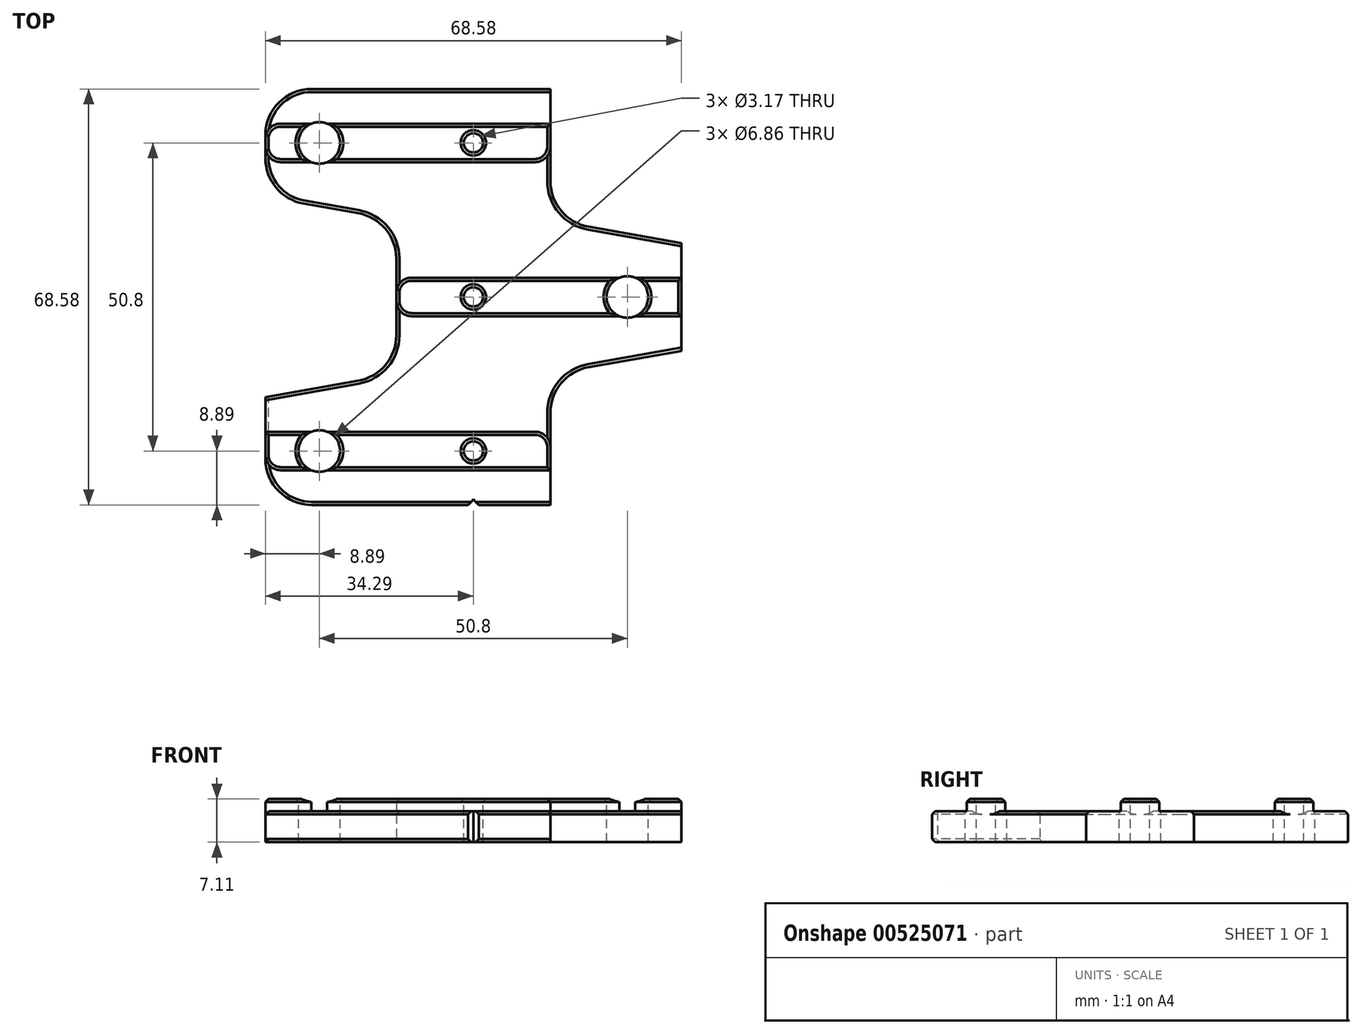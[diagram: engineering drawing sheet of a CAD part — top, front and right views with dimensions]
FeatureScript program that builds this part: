
annotation { "Feature Type Name" : "Feature", "Feature Type Description" : "" }
export const myFeature = defineFeature(function(context is Context, id is Id, definition is map)
    precondition{}
    {
        {
            var Q0;
            Q0=qCreatedBy(makeId("Right.planeOp"),FACE);
            var sketch = newSketch(context, id + "F0", { "sketchPlane" : qUnion([Q0])});
            skLineSegment(sketch, "E0.bottom", {"start": v(-34.3, 5.08) * mm, "end": v(-28.58, 5.08) * mm});
            skLineSegment(sketch, "E0.top", {"start": v(-34.3, 0) * mm, "end": v(34.3, 0) * mm});
            skLineSegment(sketch, "E0.left", {"start": v(-34.3, 5.08) * mm, "end": v(-34.3, 0) * mm});
            skLineSegment(sketch, "E0.right", {"start": v(34.3, 5.08) * mm, "end": v(34.3, 0) * mm});
            skLineSegment(sketch, "E1.bottom", {"start": v(-3.18, 7.11) * mm, "end": v(3.18, 7.11) * mm});
            skLineSegment(sketch, "E1.left", {"start": v(-3.18, 7.11) * mm, "end": v(-3.18, 5.08) * mm});
            skLineSegment(sketch, "E1.right", {"start": v(3.18, 7.11) * mm, "end": v(3.18, 5.08) * mm});
            skLineSegment(sketch, "E2.bottom", {"start": v(22.23, 7.11) * mm, "end": v(28.58, 7.11) * mm});
            skLineSegment(sketch, "E2.left", {"start": v(22.23, 7.11) * mm, "end": v(22.23, 5.08) * mm});
            skLineSegment(sketch, "E2.right", {"start": v(28.58, 7.11) * mm, "end": v(28.58, 5.08) * mm});
            skLineSegment(sketch, "E3.bottom", {"start": v(-28.58, 7.11) * mm, "end": v(-22.23, 7.11) * mm});
            skLineSegment(sketch, "E3.left", {"start": v(-28.58, 7.11) * mm, "end": v(-28.58, 5.08) * mm});
            skLineSegment(sketch, "E3.right", {"start": v(-22.23, 7.11) * mm, "end": v(-22.23, 5.08) * mm});
            skLineSegment(sketch, "E4.trimOffspring", {"start": v(-22.23, 5.08) * mm, "end": v(-3.18, 5.08) * mm});
            skLineSegment(sketch, "E5.trimOffspring", {"start": v(3.18, 5.08) * mm, "end": v(22.23, 5.08) * mm});
            skLineSegment(sketch, "E6.trimOffspring", {"start": v(28.58, 5.08) * mm, "end": v(34.3, 5.08) * mm});
            skSolve(sketch);
        }
        {
            var Q0;
            Q0 = qSketchRegion(id + "F0", true);
            extrude(context, id + "F1", {"entities" : qUnion([Q0]), "endBound" : BoundingType.SYMMETRIC, "depth" : 68.58 * mm, "offsetDistance" : 25.4 * mm, "hasSecondDirection" : true, "secondDirectionOppositeDirection" : true, "secondDirectionDepth" : 25.4 * mm});
        }
        {
            var Q0;
            Q0=qCreatedBy(makeId("Top.planeOp"),FACE);
            var sketch = newSketch(context, id + "F2", { "sketchPlane" : qUnion([Q0])});
            skLineSegment(sketch, "E7", {"start": v(-34.3, 16.51) * mm, "end": v(-12.7, 12.7) * mm});
            skLineSegment(sketch, "E8", {"start": v(-12.7, 12.7) * mm, "end": v(-12.7, -12.7) * mm});
            skLineSegment(sketch, "E9", {"start": v(-12.7, -12.7) * mm, "end": v(-34.3, -16.51) * mm});
            skLineSegment(sketch, "E10", {"start": v(-34.3, -16.51) * mm, "end": v(-34.3, 16.51) * mm});
            skSolve(sketch);
        }
        {
            var Q0;
            Q0 = qSketchRegion(id + "F2", true);
            extrude(context, id + "F3", {"entities" : qUnion([Q0]), "operationType" : NewBodyOperationType.REMOVE, "endBound" : BoundingType.THROUGH_ALL, "depth" : 25.4 * mm, "offsetDistance" : 25.4 * mm});
        }
        {
            var Q0;
            Q0=qCreatedBy(makeId("Top.planeOp"),FACE);
            var sketch = newSketch(context, id + "F4", { "sketchPlane" : qUnion([Q0])});
            skLineSegment(sketch, "E11", {"start": v(34.62, 34.3) * mm, "end": v(12.7, 34.3) * mm});
            skLineSegment(sketch, "E12", {"start": v(12.7, 34.3) * mm, "end": v(12.7, 12.7) * mm});
            skLineSegment(sketch, "E13", {"start": v(12.7, 12.7) * mm, "end": v(34.3, 8.9) * mm});
            skLineSegment(sketch, "E14", {"start": v(34.3, 8.9) * mm, "end": v(34.3, -8.9) * mm});
            skLineSegment(sketch, "E15", {"start": v(34.3, -8.9) * mm, "end": v(12.7, -12.7) * mm});
            skLineSegment(sketch, "E16", {"start": v(12.7, -12.7) * mm, "end": v(12.7, -34.3) * mm});
            skLineSegment(sketch, "E17", {"start": v(12.7, -34.3) * mm, "end": v(34.62, -34.3) * mm});
            skLineSegment(sketch, "E18", {"start": v(34.62, -34.3) * mm, "end": v(34.62, 34.3) * mm});
            skSolve(sketch);
        }
        {
            var Q0;
            Q0 = qSketchRegion(id + "F4", true);
            extrude(context, id + "F5", {"entities" : qUnion([Q0]), "operationType" : NewBodyOperationType.REMOVE, "endBound" : BoundingType.THROUGH_ALL, "depth" : 25.4 * mm, "offsetDistance" : 25.4 * mm});
        }
        {
            var Q0;
            Q0=makeQuery(id+"F1.opExtrude","SWEPT_FACE",FACE,{"disambiguationData":[OSD([sQuery(id+"F0.wireOp",EDGE,"E1.bottom")])]});
            var sketch = newSketch(context, id + "F6", { "sketchPlane" : qUnion([Q0])});
            skPoint(sketch, "E19", {"position": v(0, 0) * mm});
            skPoint(sketch, "E20", {"position": v(0, 25.4) * mm});
            skPoint(sketch, "E21", {"position": v(0, -25.4) * mm});
            skLineSegment(sketch, "E22", {"start": v(-34.3, 25.4) * mm, "end": v(12.7, 25.4) * mm, "construction": true});
            skLineSegment(sketch, "E23", {"start": v(-34.3, -25.4) * mm, "end": v(12.7, -25.4) * mm, "construction": true});
            skPoint(sketch, "E24", {"position": v(-25.4, 25.4) * mm});
            skPoint(sketch, "E25", {"position": v(25.4, 0) * mm});
            skPoint(sketch, "E26", {"position": v(-25.4, -25.4) * mm});
            skSolve(sketch);
        }
        {
            var Q0;
            Q0=sQuery(id+"F6.wireOp",VERTEX,"E20");
            var Q1;
            Q1=sQuery(id+"F6.wireOp",VERTEX,"E19");
            var Q2;
            Q2=sQuery(id+"F6.wireOp",VERTEX,"E21");
            var Q3;
            Q3=makeQuery(id+"F1.opExtrude","SWEPT_BODY",BODY,{"disambiguationData":[OSD([sQuery(id+"F0.wireOp",EDGE,"E0.bottom"),sQuery(id+"F0.wireOp",EDGE,"E0.top"),sQuery(id+"F0.wireOp",EDGE,"E0.left"),sQuery(id+"F0.wireOp",EDGE,"E0.right"),sQuery(id+"F0.wireOp",EDGE,"E1.bottom"),sQuery(id+"F0.wireOp",EDGE,"E1.left"),sQuery(id+"F0.wireOp",EDGE,"E1.right"),sQuery(id+"F0.wireOp",EDGE,"E2.bottom"),sQuery(id+"F0.wireOp",EDGE,"E2.left"),sQuery(id+"F0.wireOp",EDGE,"E2.right"),sQuery(id+"F0.wireOp",EDGE,"E3.bottom"),sQuery(id+"F0.wireOp",EDGE,"E3.left"),sQuery(id+"F0.wireOp",EDGE,"E3.right"),sQuery(id+"F0.wireOp",EDGE,"E4.trimOffspring"),sQuery(id+"F0.wireOp",EDGE,"E5.trimOffspring"),sQuery(id+"F0.wireOp",EDGE,"E6.trimOffspring")])]});
            hole(context, id + "F7", {"style" : HoleStyle.SIMPLE, "endStyle" : HoleEndStyle.THROUGH, "holeDiameter" : 3.17 * mm, "tappedDepth" : 12.7 * mm, "tapClearance" : 3, "startFromSketch" : true, "locations" : qUnion([Q0, Q1, Q2]), "scope" : qUnion([Q3])});
        }
        {
            var Q0;
            Q0=sQuery(id+"F6.wireOp",VERTEX,"E24");
            var Q1;
            Q1=sQuery(id+"F6.wireOp",VERTEX,"E25");
            var Q2;
            Q2=sQuery(id+"F6.wireOp",VERTEX,"E26");
            var Q3;
            Q3=makeQuery(id+"F1.opExtrude","SWEPT_BODY",BODY,{"disambiguationData":[OSD([sQuery(id+"F0.wireOp",EDGE,"E0.bottom"),sQuery(id+"F0.wireOp",EDGE,"E0.top"),sQuery(id+"F0.wireOp",EDGE,"E0.left"),sQuery(id+"F0.wireOp",EDGE,"E0.right"),sQuery(id+"F0.wireOp",EDGE,"E1.bottom"),sQuery(id+"F0.wireOp",EDGE,"E1.left"),sQuery(id+"F0.wireOp",EDGE,"E1.right"),sQuery(id+"F0.wireOp",EDGE,"E2.bottom"),sQuery(id+"F0.wireOp",EDGE,"E2.left"),sQuery(id+"F0.wireOp",EDGE,"E2.right"),sQuery(id+"F0.wireOp",EDGE,"E3.bottom"),sQuery(id+"F0.wireOp",EDGE,"E3.left"),sQuery(id+"F0.wireOp",EDGE,"E3.right"),sQuery(id+"F0.wireOp",EDGE,"E4.trimOffspring"),sQuery(id+"F0.wireOp",EDGE,"E5.trimOffspring"),sQuery(id+"F0.wireOp",EDGE,"E6.trimOffspring")])]});
            hole(context, id + "F8", {"style" : HoleStyle.SIMPLE, "endStyle" : HoleEndStyle.THROUGH, "holeDiameter" : 6.86 * mm, "tappedDepth" : 12.7 * mm, "tapClearance" : 3, "startFromSketch" : true, "locations" : qUnion([Q0, Q1, Q2]), "scope" : qUnion([Q3])});
        }
        {
            var Q0;
            Q0=makeQuery(id+"F3.boolean.opBoolean","COPY",EDGE,{"derivedFrom":makeQuery(id+"F3.opExtrude","SWEPT_EDGE",EDGE,{"disambiguationData":[OSD([sQuery(id+"F2.wireOp",EDGE,"E8"),sQuery(id+"F2.wireOp",EDGE,"E9")])]})});
            var Q1;
            Q1=makeQuery(id+"F3.boolean.opBoolean","COPY",EDGE,{"derivedFrom":makeQuery(id+"F3.opExtrude","SWEPT_EDGE",EDGE,{"disambiguationData":[OSD([sQuery(id+"F2.wireOp",EDGE,"E9"),sQuery(id+"F2.wireOp",EDGE,"E10")])]})});
            var Q2;
            Q2=makeQuery(id+"F1.opExtrude","CAP_EDGE",EDGE,{"disambiguationData":[OSD([sQuery(id+"F0.wireOp",EDGE,"E0.left")])],"isStart":true});
            var Q3;
            Q3=makeQuery(id+"F3.boolean.opBoolean","COPY",EDGE,{"derivedFrom":makeQuery(id+"F3.opExtrude","SWEPT_EDGE",EDGE,{"disambiguationData":[OSD([sQuery(id+"F2.wireOp",EDGE,"E7"),sQuery(id+"F2.wireOp",EDGE,"E10")])]})});
            var Q4;
            Q4=makeQuery(id+"F1.opExtrude","CAP_EDGE",EDGE,{"disambiguationData":[OSD([sQuery(id+"F0.wireOp",EDGE,"E0.right")])],"isStart":true});
            var Q5;
            Q5=makeQuery(id+"F5.boolean.opBoolean","COPY",EDGE,{"derivedFrom":makeQuery(id+"F5.opExtrude","SWEPT_EDGE",EDGE,{"disambiguationData":[OSD([sQuery(id+"F4.wireOp",EDGE,"E11"),sQuery(id+"F4.wireOp",EDGE,"E12")])]})});
            var Q6;
            Q6=makeQuery(id+"F5.boolean.opBoolean","COPY",EDGE,{"derivedFrom":makeQuery(id+"F5.opExtrude","SWEPT_EDGE",EDGE,{"disambiguationData":[OSD([sQuery(id+"F4.wireOp",EDGE,"E13"),sQuery(id+"F4.wireOp",EDGE,"E14")])]})});
            var Q7;
            Q7=makeQuery(id+"F5.boolean.opBoolean","COPY",EDGE,{"derivedFrom":makeQuery(id+"F5.opExtrude","SWEPT_EDGE",EDGE,{"disambiguationData":[OSD([sQuery(id+"F4.wireOp",EDGE,"E12"),sQuery(id+"F4.wireOp",EDGE,"E13")])]})});
            var Q8;
            Q8=makeQuery(id+"F5.boolean.opBoolean","COPY",EDGE,{"derivedFrom":makeQuery(id+"F5.opExtrude","SWEPT_EDGE",EDGE,{"disambiguationData":[OSD([sQuery(id+"F4.wireOp",EDGE,"E16"),sQuery(id+"F4.wireOp",EDGE,"E17")])]})});
            var Q9;
            Q9=makeQuery(id+"F5.boolean.opBoolean","COPY",EDGE,{"derivedFrom":makeQuery(id+"F5.opExtrude","SWEPT_EDGE",EDGE,{"disambiguationData":[OSD([sQuery(id+"F4.wireOp",EDGE,"E15"),sQuery(id+"F4.wireOp",EDGE,"E16")])]})});
            var Q10;
            Q10=makeQuery(id+"F5.boolean.opBoolean","COPY",EDGE,{"derivedFrom":makeQuery(id+"F5.opExtrude","SWEPT_EDGE",EDGE,{"disambiguationData":[OSD([sQuery(id+"F4.wireOp",EDGE,"E14"),sQuery(id+"F4.wireOp",EDGE,"E15")])]})});
            var Q11;
            Q11=makeQuery(id+"F3.boolean.opBoolean","COPY",EDGE,{"derivedFrom":makeQuery(id+"F3.opExtrude","SWEPT_EDGE",EDGE,{"disambiguationData":[OSD([sQuery(id+"F2.wireOp",EDGE,"E7"),sQuery(id+"F2.wireOp",EDGE,"E8")])]})});
            fillet(context, id + "F9", {"entities" : qUnion([Q0, Q1, Q2, Q3, Q4, Q5, Q6, Q7, Q8, Q9, Q10, Q11]), "radius" : 7.62 * mm, "tangentPropagation" : true, "allowEdgeOverflow" : false});
        }
        {
            var Q0;
            {var subQ0=sQuery(id+"F4.wireOp",EDGE,"E16");Q0=makeQuery(id+"F9.opFillet","BLEND_EDGE",EDGE,{"blendedFrom":[makeQuery(id+"F5.boolean.opBoolean","COPY",EDGE,{"derivedFrom":makeQuery(id+"F5.opExtrude","SWEPT_EDGE",EDGE,{"disambiguationData":[OSD([subQ0,sQuery(id+"F4.wireOp",EDGE,"E17")])]})}),makeQuery(id+"F8.hole-2.boolean.opBoolean","SPLIT",FACE,{"disambiguationData":[TD([makeQuery(id+"F5.boolean.opBoolean","COPY",FACE,{"derivedFrom":makeQuery(id+"F5.opExtrude","SWEPT_FACE",FACE,{"disambiguationData":[OSD([subQ0])]})})])],"derivedFrom":makeQuery(id+"F1.opExtrude","SWEPT_FACE",FACE,{"disambiguationData":[OSD([sQuery(id+"F0.wireOp",EDGE,"E3.left")])]})})],"blendedInto":[makeQuery(id+"F8.hole-2.boolean.opBoolean","SPLIT",FACE,{"disambiguationData":[TD([makeQuery(id+"F5.boolean.opBoolean","COPY",FACE,{"derivedFrom":makeQuery(id+"F5.opExtrude","SWEPT_FACE",FACE,{"disambiguationData":[OSD([subQ0])]})})])],"derivedFrom":makeQuery(id+"F1.opExtrude","SWEPT_FACE",FACE,{"disambiguationData":[OSD([sQuery(id+"F0.wireOp",EDGE,"E3.left")])]})})]});}
            var Q1;
            Q1=makeQuery(id+"F5.boolean.opBoolean","INTERSECT",EDGE,{"derivedFrom":[makeQuery(id+"F1.opExtrude","SWEPT_FACE",FACE,{"disambiguationData":[OSD([sQuery(id+"F0.wireOp",EDGE,"E3.right")])]}),makeQuery(id+"F5.opExtrude","SWEPT_FACE",FACE,{"disambiguationData":[OSD([sQuery(id+"F4.wireOp",EDGE,"E16")])]})]});
            var Q2;
            {var subQ0=sQuery(id+"F0.wireOp",EDGE,"E4.trimOffspring");var subQ1=sQuery(id+"F0.wireOp",EDGE,"E1.left");var subQ2=sQuery(id+"F0.wireOp",EDGE,"E1.bottom");Q2=makeQuery(id+"F9.opFillet","BLEND_EDGE",EDGE,{"blendedFrom":[makeQuery(id+"F5.boolean.opBoolean","COPY",EDGE,{"derivedFrom":makeQuery(id+"F5.opExtrude","SWEPT_EDGE",EDGE,{"disambiguationData":[OSD([sQuery(id+"F4.wireOp",EDGE,"E14"),sQuery(id+"F4.wireOp",EDGE,"E15")])]})}),makeQuery(id+"F8.hole-1.boolean.opBoolean","SPLIT",FACE,{"disambiguationData":[TD([makeQuery(id+"F1.opExtrude","CAP_FACE",FACE,{"disambiguationData":[OSD([sQuery(id+"F0.wireOp",EDGE,"E0.bottom"),sQuery(id+"F0.wireOp",EDGE,"E0.top"),sQuery(id+"F0.wireOp",EDGE,"E0.left"),sQuery(id+"F0.wireOp",EDGE,"E0.right"),subQ2,subQ1,sQuery(id+"F0.wireOp",EDGE,"E1.right"),sQuery(id+"F0.wireOp",EDGE,"E2.bottom"),sQuery(id+"F0.wireOp",EDGE,"E2.left"),sQuery(id+"F0.wireOp",EDGE,"E2.right"),sQuery(id+"F0.wireOp",EDGE,"E3.bottom"),sQuery(id+"F0.wireOp",EDGE,"E3.left"),sQuery(id+"F0.wireOp",EDGE,"E3.right"),subQ0,sQuery(id+"F0.wireOp",EDGE,"E5.trimOffspring"),sQuery(id+"F0.wireOp",EDGE,"E6.trimOffspring")])],"isStart":false})])],"derivedFrom":makeQuery(id+"F1.opExtrude","SWEPT_FACE",FACE,{"disambiguationData":[OSD([subQ1])]})})],"blendedInto":[makeQuery(id+"F8.hole-1.boolean.opBoolean","SPLIT",FACE,{"disambiguationData":[TD([makeQuery(id+"F1.opExtrude","CAP_FACE",FACE,{"disambiguationData":[OSD([sQuery(id+"F0.wireOp",EDGE,"E0.bottom"),sQuery(id+"F0.wireOp",EDGE,"E0.top"),sQuery(id+"F0.wireOp",EDGE,"E0.left"),sQuery(id+"F0.wireOp",EDGE,"E0.right"),subQ2,subQ1,sQuery(id+"F0.wireOp",EDGE,"E1.right"),sQuery(id+"F0.wireOp",EDGE,"E2.bottom"),sQuery(id+"F0.wireOp",EDGE,"E2.left"),sQuery(id+"F0.wireOp",EDGE,"E2.right"),sQuery(id+"F0.wireOp",EDGE,"E3.bottom"),sQuery(id+"F0.wireOp",EDGE,"E3.left"),sQuery(id+"F0.wireOp",EDGE,"E3.right"),subQ0,sQuery(id+"F0.wireOp",EDGE,"E5.trimOffspring"),sQuery(id+"F0.wireOp",EDGE,"E6.trimOffspring")])],"isStart":false})])],"derivedFrom":makeQuery(id+"F1.opExtrude","SWEPT_FACE",FACE,{"disambiguationData":[OSD([subQ1])]})})]});}
            var Q3;
            {var subQ0=sQuery(id+"F0.wireOp",EDGE,"E5.trimOffspring");var subQ1=sQuery(id+"F0.wireOp",EDGE,"E1.right");var subQ2=sQuery(id+"F0.wireOp",EDGE,"E1.bottom");Q3=makeQuery(id+"F9.opFillet","BLEND_EDGE",EDGE,{"blendedFrom":[makeQuery(id+"F5.boolean.opBoolean","COPY",EDGE,{"derivedFrom":makeQuery(id+"F5.opExtrude","SWEPT_EDGE",EDGE,{"disambiguationData":[OSD([sQuery(id+"F4.wireOp",EDGE,"E13"),sQuery(id+"F4.wireOp",EDGE,"E14")])]})}),makeQuery(id+"F8.hole-1.boolean.opBoolean","SPLIT",FACE,{"disambiguationData":[TD([makeQuery(id+"F1.opExtrude","CAP_FACE",FACE,{"disambiguationData":[OSD([sQuery(id+"F0.wireOp",EDGE,"E0.bottom"),sQuery(id+"F0.wireOp",EDGE,"E0.top"),sQuery(id+"F0.wireOp",EDGE,"E0.left"),sQuery(id+"F0.wireOp",EDGE,"E0.right"),subQ2,sQuery(id+"F0.wireOp",EDGE,"E1.left"),subQ1,sQuery(id+"F0.wireOp",EDGE,"E2.bottom"),sQuery(id+"F0.wireOp",EDGE,"E2.left"),sQuery(id+"F0.wireOp",EDGE,"E2.right"),sQuery(id+"F0.wireOp",EDGE,"E3.bottom"),sQuery(id+"F0.wireOp",EDGE,"E3.left"),sQuery(id+"F0.wireOp",EDGE,"E3.right"),sQuery(id+"F0.wireOp",EDGE,"E4.trimOffspring"),subQ0,sQuery(id+"F0.wireOp",EDGE,"E6.trimOffspring")])],"isStart":false})])],"derivedFrom":makeQuery(id+"F1.opExtrude","SWEPT_FACE",FACE,{"disambiguationData":[OSD([subQ1])]})})],"blendedInto":[makeQuery(id+"F8.hole-1.boolean.opBoolean","SPLIT",FACE,{"disambiguationData":[TD([makeQuery(id+"F1.opExtrude","CAP_FACE",FACE,{"disambiguationData":[OSD([sQuery(id+"F0.wireOp",EDGE,"E0.bottom"),sQuery(id+"F0.wireOp",EDGE,"E0.top"),sQuery(id+"F0.wireOp",EDGE,"E0.left"),sQuery(id+"F0.wireOp",EDGE,"E0.right"),subQ2,sQuery(id+"F0.wireOp",EDGE,"E1.left"),subQ1,sQuery(id+"F0.wireOp",EDGE,"E2.bottom"),sQuery(id+"F0.wireOp",EDGE,"E2.left"),sQuery(id+"F0.wireOp",EDGE,"E2.right"),sQuery(id+"F0.wireOp",EDGE,"E3.bottom"),sQuery(id+"F0.wireOp",EDGE,"E3.left"),sQuery(id+"F0.wireOp",EDGE,"E3.right"),sQuery(id+"F0.wireOp",EDGE,"E4.trimOffspring"),subQ0,sQuery(id+"F0.wireOp",EDGE,"E6.trimOffspring")])],"isStart":false})])],"derivedFrom":makeQuery(id+"F1.opExtrude","SWEPT_FACE",FACE,{"disambiguationData":[OSD([subQ1])]})})]});}
            var Q4;
            Q4=makeQuery(id+"F8.hole-1.boolean.opBoolean","INTERSECT",EDGE,{"disambiguationData":[OD(1.0)],"derivedFrom":[makeQuery(id+"F1.opExtrude","SWEPT_FACE",FACE,{"disambiguationData":[OSD([sQuery(id+"F0.wireOp",EDGE,"E1.left")])]}),makeQuery(id+"F8.hole-1.opRevolve","SWEPT_FACE",FACE,{"disambiguationData":[OSD([sQuery(id+"F8.hole-1.sketch.wireOp",EDGE,"core_line_2")])]})]});
            var Q5;
            Q5=makeQuery(id+"F8.hole-1.boolean.opBoolean","INTERSECT",EDGE,{"disambiguationData":[OD(0.0)],"derivedFrom":[makeQuery(id+"F1.opExtrude","SWEPT_FACE",FACE,{"disambiguationData":[OSD([sQuery(id+"F0.wireOp",EDGE,"E1.left")])]}),makeQuery(id+"F8.hole-1.opRevolve","SWEPT_FACE",FACE,{"disambiguationData":[OSD([sQuery(id+"F8.hole-1.sketch.wireOp",EDGE,"core_line_2")])]})]});
            var Q6;
            Q6=makeQuery(id+"F8.hole-0.boolean.opBoolean","INTERSECT",EDGE,{"disambiguationData":[OD(1.0)],"derivedFrom":[makeQuery(id+"F1.opExtrude","SWEPT_FACE",FACE,{"disambiguationData":[OSD([sQuery(id+"F0.wireOp",EDGE,"E2.right")])]}),makeQuery(id+"F8.hole-0.opRevolve","SWEPT_FACE",FACE,{"disambiguationData":[OSD([sQuery(id+"F8.hole-0.sketch.wireOp",EDGE,"core_line_2")])]})]});
            var Q7;
            Q7=makeQuery(id+"F8.hole-0.boolean.opBoolean","INTERSECT",EDGE,{"disambiguationData":[OD(1.0)],"derivedFrom":[makeQuery(id+"F1.opExtrude","SWEPT_FACE",FACE,{"disambiguationData":[OSD([sQuery(id+"F0.wireOp",EDGE,"E2.left")])]}),makeQuery(id+"F8.hole-0.opRevolve","SWEPT_FACE",FACE,{"disambiguationData":[OSD([sQuery(id+"F8.hole-0.sketch.wireOp",EDGE,"core_line_2")])]})]});
            var Q8;
            Q8=makeQuery(id+"F8.hole-0.boolean.opBoolean","INTERSECT",EDGE,{"disambiguationData":[OD(0.0)],"derivedFrom":[makeQuery(id+"F1.opExtrude","SWEPT_FACE",FACE,{"disambiguationData":[OSD([sQuery(id+"F0.wireOp",EDGE,"E2.left")])]}),makeQuery(id+"F8.hole-0.opRevolve","SWEPT_FACE",FACE,{"disambiguationData":[OSD([sQuery(id+"F8.hole-0.sketch.wireOp",EDGE,"core_line_2")])]})]});
            var Q9;
            Q9=makeQuery(id+"F8.hole-0.boolean.opBoolean","INTERSECT",EDGE,{"disambiguationData":[OD(0.0)],"derivedFrom":[makeQuery(id+"F1.opExtrude","SWEPT_FACE",FACE,{"disambiguationData":[OSD([sQuery(id+"F0.wireOp",EDGE,"E2.right")])]}),makeQuery(id+"F8.hole-0.opRevolve","SWEPT_FACE",FACE,{"disambiguationData":[OSD([sQuery(id+"F8.hole-0.sketch.wireOp",EDGE,"core_line_2")])]})]});
            var Q10;
            {var subQ0=sQuery(id+"F0.wireOp",EDGE,"E6.trimOffspring");var subQ1=sQuery(id+"F0.wireOp",EDGE,"E2.right");var subQ2=sQuery(id+"F0.wireOp",EDGE,"E2.bottom");var subQ3=sQuery(id+"F0.wireOp",EDGE,"E0.right");Q10=makeQuery(id+"F9.opFillet","BLEND_EDGE",EDGE,{"blendedFrom":[makeQuery(id+"F1.opExtrude","CAP_EDGE",EDGE,{"disambiguationData":[OSD([subQ3])],"isStart":true}),makeQuery(id+"F8.hole-0.boolean.opBoolean","SPLIT",FACE,{"disambiguationData":[TD([makeQuery(id+"F1.opExtrude","CAP_FACE",FACE,{"disambiguationData":[OSD([sQuery(id+"F0.wireOp",EDGE,"E0.bottom"),sQuery(id+"F0.wireOp",EDGE,"E0.top"),sQuery(id+"F0.wireOp",EDGE,"E0.left"),subQ3,sQuery(id+"F0.wireOp",EDGE,"E1.bottom"),sQuery(id+"F0.wireOp",EDGE,"E1.left"),sQuery(id+"F0.wireOp",EDGE,"E1.right"),subQ2,sQuery(id+"F0.wireOp",EDGE,"E2.left"),subQ1,sQuery(id+"F0.wireOp",EDGE,"E3.bottom"),sQuery(id+"F0.wireOp",EDGE,"E3.left"),sQuery(id+"F0.wireOp",EDGE,"E3.right"),sQuery(id+"F0.wireOp",EDGE,"E4.trimOffspring"),sQuery(id+"F0.wireOp",EDGE,"E5.trimOffspring"),subQ0])],"isStart":true})])],"derivedFrom":makeQuery(id+"F1.opExtrude","SWEPT_FACE",FACE,{"disambiguationData":[OSD([subQ1])]})})],"blendedInto":[makeQuery(id+"F8.hole-0.boolean.opBoolean","SPLIT",FACE,{"disambiguationData":[TD([makeQuery(id+"F1.opExtrude","CAP_FACE",FACE,{"disambiguationData":[OSD([sQuery(id+"F0.wireOp",EDGE,"E0.bottom"),sQuery(id+"F0.wireOp",EDGE,"E0.top"),sQuery(id+"F0.wireOp",EDGE,"E0.left"),subQ3,sQuery(id+"F0.wireOp",EDGE,"E1.bottom"),sQuery(id+"F0.wireOp",EDGE,"E1.left"),sQuery(id+"F0.wireOp",EDGE,"E1.right"),subQ2,sQuery(id+"F0.wireOp",EDGE,"E2.left"),subQ1,sQuery(id+"F0.wireOp",EDGE,"E3.bottom"),sQuery(id+"F0.wireOp",EDGE,"E3.left"),sQuery(id+"F0.wireOp",EDGE,"E3.right"),sQuery(id+"F0.wireOp",EDGE,"E4.trimOffspring"),sQuery(id+"F0.wireOp",EDGE,"E5.trimOffspring"),subQ0])],"isStart":true})])],"derivedFrom":makeQuery(id+"F1.opExtrude","SWEPT_FACE",FACE,{"disambiguationData":[OSD([subQ1])]})})]});}
            var Q11;
            {var subQ0=sQuery(id+"F4.wireOp",EDGE,"E12");Q11=makeQuery(id+"F9.opFillet","BLEND_EDGE",EDGE,{"blendedFrom":[makeQuery(id+"F5.boolean.opBoolean","COPY",EDGE,{"derivedFrom":makeQuery(id+"F5.opExtrude","SWEPT_EDGE",EDGE,{"disambiguationData":[OSD([sQuery(id+"F4.wireOp",EDGE,"E11"),subQ0])]})}),makeQuery(id+"F8.hole-0.boolean.opBoolean","SPLIT",FACE,{"disambiguationData":[TD([makeQuery(id+"F5.boolean.opBoolean","COPY",FACE,{"derivedFrom":makeQuery(id+"F5.opExtrude","SWEPT_FACE",FACE,{"disambiguationData":[OSD([subQ0])]})})])],"derivedFrom":makeQuery(id+"F1.opExtrude","SWEPT_FACE",FACE,{"disambiguationData":[OSD([sQuery(id+"F0.wireOp",EDGE,"E2.right")])]})})],"blendedInto":[makeQuery(id+"F8.hole-0.boolean.opBoolean","SPLIT",FACE,{"disambiguationData":[TD([makeQuery(id+"F5.boolean.opBoolean","COPY",FACE,{"derivedFrom":makeQuery(id+"F5.opExtrude","SWEPT_FACE",FACE,{"disambiguationData":[OSD([subQ0])]})})])],"derivedFrom":makeQuery(id+"F1.opExtrude","SWEPT_FACE",FACE,{"disambiguationData":[OSD([sQuery(id+"F0.wireOp",EDGE,"E2.right")])]})})]});}
            var Q12;
            Q12=makeQuery(id+"F5.boolean.opBoolean","INTERSECT",EDGE,{"derivedFrom":[makeQuery(id+"F1.opExtrude","SWEPT_FACE",FACE,{"disambiguationData":[OSD([sQuery(id+"F0.wireOp",EDGE,"E2.left")])]}),makeQuery(id+"F5.opExtrude","SWEPT_FACE",FACE,{"disambiguationData":[OSD([sQuery(id+"F4.wireOp",EDGE,"E12")])]})]});
            var Q13;
            {var subQ0=sQuery(id+"F0.wireOp",EDGE,"E5.trimOffspring");var subQ1=sQuery(id+"F0.wireOp",EDGE,"E2.left");var subQ2=sQuery(id+"F0.wireOp",EDGE,"E2.bottom");Q13=makeQuery(id+"F9.opFillet","BLEND_EDGE",EDGE,{"blendedFrom":[makeQuery(id+"F3.boolean.opBoolean","COPY",EDGE,{"derivedFrom":makeQuery(id+"F3.opExtrude","SWEPT_EDGE",EDGE,{"disambiguationData":[OSD([sQuery(id+"F2.wireOp",EDGE,"E7"),sQuery(id+"F2.wireOp",EDGE,"E10")])]})}),makeQuery(id+"F8.hole-0.boolean.opBoolean","SPLIT",FACE,{"disambiguationData":[TD([makeQuery(id+"F1.opExtrude","CAP_FACE",FACE,{"disambiguationData":[OSD([sQuery(id+"F0.wireOp",EDGE,"E0.bottom"),sQuery(id+"F0.wireOp",EDGE,"E0.top"),sQuery(id+"F0.wireOp",EDGE,"E0.left"),sQuery(id+"F0.wireOp",EDGE,"E0.right"),sQuery(id+"F0.wireOp",EDGE,"E1.bottom"),sQuery(id+"F0.wireOp",EDGE,"E1.left"),sQuery(id+"F0.wireOp",EDGE,"E1.right"),subQ2,subQ1,sQuery(id+"F0.wireOp",EDGE,"E2.right"),sQuery(id+"F0.wireOp",EDGE,"E3.bottom"),sQuery(id+"F0.wireOp",EDGE,"E3.left"),sQuery(id+"F0.wireOp",EDGE,"E3.right"),sQuery(id+"F0.wireOp",EDGE,"E4.trimOffspring"),subQ0,sQuery(id+"F0.wireOp",EDGE,"E6.trimOffspring")])],"isStart":true})])],"derivedFrom":makeQuery(id+"F1.opExtrude","SWEPT_FACE",FACE,{"disambiguationData":[OSD([subQ1])]})})],"blendedInto":[makeQuery(id+"F8.hole-0.boolean.opBoolean","SPLIT",FACE,{"disambiguationData":[TD([makeQuery(id+"F1.opExtrude","CAP_FACE",FACE,{"disambiguationData":[OSD([sQuery(id+"F0.wireOp",EDGE,"E0.bottom"),sQuery(id+"F0.wireOp",EDGE,"E0.top"),sQuery(id+"F0.wireOp",EDGE,"E0.left"),sQuery(id+"F0.wireOp",EDGE,"E0.right"),sQuery(id+"F0.wireOp",EDGE,"E1.bottom"),sQuery(id+"F0.wireOp",EDGE,"E1.left"),sQuery(id+"F0.wireOp",EDGE,"E1.right"),subQ2,subQ1,sQuery(id+"F0.wireOp",EDGE,"E2.right"),sQuery(id+"F0.wireOp",EDGE,"E3.bottom"),sQuery(id+"F0.wireOp",EDGE,"E3.left"),sQuery(id+"F0.wireOp",EDGE,"E3.right"),sQuery(id+"F0.wireOp",EDGE,"E4.trimOffspring"),subQ0,sQuery(id+"F0.wireOp",EDGE,"E6.trimOffspring")])],"isStart":true})])],"derivedFrom":makeQuery(id+"F1.opExtrude","SWEPT_FACE",FACE,{"disambiguationData":[OSD([subQ1])]})})]});}
            var Q14;
            Q14=makeQuery(id+"F3.boolean.opBoolean","INTERSECT",EDGE,{"derivedFrom":[makeQuery(id+"F1.opExtrude","SWEPT_FACE",FACE,{"disambiguationData":[OSD([sQuery(id+"F0.wireOp",EDGE,"E1.right")])]}),makeQuery(id+"F3.opExtrude","SWEPT_FACE",FACE,{"disambiguationData":[OSD([sQuery(id+"F2.wireOp",EDGE,"E8")])]})]});
            var Q15;
            Q15=makeQuery(id+"F3.boolean.opBoolean","INTERSECT",EDGE,{"derivedFrom":[makeQuery(id+"F1.opExtrude","SWEPT_FACE",FACE,{"disambiguationData":[OSD([sQuery(id+"F0.wireOp",EDGE,"E1.left")])]}),makeQuery(id+"F3.opExtrude","SWEPT_FACE",FACE,{"disambiguationData":[OSD([sQuery(id+"F2.wireOp",EDGE,"E8")])]})]});
            var Q16;
            Q16=makeQuery(id+"F8.hole-2.boolean.opBoolean","INTERSECT",EDGE,{"disambiguationData":[OD(1.0)],"derivedFrom":[makeQuery(id+"F1.opExtrude","SWEPT_FACE",FACE,{"disambiguationData":[OSD([sQuery(id+"F0.wireOp",EDGE,"E3.right")])]}),makeQuery(id+"F8.hole-2.opRevolve","SWEPT_FACE",FACE,{"disambiguationData":[OSD([sQuery(id+"F8.hole-2.sketch.wireOp",EDGE,"core_line_2")])]})]});
            var Q17;
            Q17=makeQuery(id+"F8.hole-2.boolean.opBoolean","INTERSECT",EDGE,{"disambiguationData":[OD(0.0)],"derivedFrom":[makeQuery(id+"F1.opExtrude","SWEPT_FACE",FACE,{"disambiguationData":[OSD([sQuery(id+"F0.wireOp",EDGE,"E3.right")])]}),makeQuery(id+"F8.hole-2.opRevolve","SWEPT_FACE",FACE,{"disambiguationData":[OSD([sQuery(id+"F8.hole-2.sketch.wireOp",EDGE,"core_line_2")])]})]});
            var Q18;
            {var subQ0=sQuery(id+"F0.wireOp",EDGE,"E4.trimOffspring");var subQ1=sQuery(id+"F0.wireOp",EDGE,"E3.right");var subQ2=sQuery(id+"F0.wireOp",EDGE,"E3.bottom");Q18=makeQuery(id+"F9.opFillet","BLEND_EDGE",EDGE,{"blendedFrom":[makeQuery(id+"F3.boolean.opBoolean","COPY",EDGE,{"derivedFrom":makeQuery(id+"F3.opExtrude","SWEPT_EDGE",EDGE,{"disambiguationData":[OSD([sQuery(id+"F2.wireOp",EDGE,"E9"),sQuery(id+"F2.wireOp",EDGE,"E10")])]})}),makeQuery(id+"F8.hole-2.boolean.opBoolean","SPLIT",FACE,{"disambiguationData":[TD([makeQuery(id+"F1.opExtrude","CAP_FACE",FACE,{"disambiguationData":[OSD([sQuery(id+"F0.wireOp",EDGE,"E0.bottom"),sQuery(id+"F0.wireOp",EDGE,"E0.top"),sQuery(id+"F0.wireOp",EDGE,"E0.left"),sQuery(id+"F0.wireOp",EDGE,"E0.right"),sQuery(id+"F0.wireOp",EDGE,"E1.bottom"),sQuery(id+"F0.wireOp",EDGE,"E1.left"),sQuery(id+"F0.wireOp",EDGE,"E1.right"),sQuery(id+"F0.wireOp",EDGE,"E2.bottom"),sQuery(id+"F0.wireOp",EDGE,"E2.left"),sQuery(id+"F0.wireOp",EDGE,"E2.right"),subQ2,sQuery(id+"F0.wireOp",EDGE,"E3.left"),subQ1,subQ0,sQuery(id+"F0.wireOp",EDGE,"E5.trimOffspring"),sQuery(id+"F0.wireOp",EDGE,"E6.trimOffspring")])],"isStart":true})])],"derivedFrom":makeQuery(id+"F1.opExtrude","SWEPT_FACE",FACE,{"disambiguationData":[OSD([subQ1])]})})],"blendedInto":[makeQuery(id+"F8.hole-2.boolean.opBoolean","SPLIT",FACE,{"disambiguationData":[TD([makeQuery(id+"F1.opExtrude","CAP_FACE",FACE,{"disambiguationData":[OSD([sQuery(id+"F0.wireOp",EDGE,"E0.bottom"),sQuery(id+"F0.wireOp",EDGE,"E0.top"),sQuery(id+"F0.wireOp",EDGE,"E0.left"),sQuery(id+"F0.wireOp",EDGE,"E0.right"),sQuery(id+"F0.wireOp",EDGE,"E1.bottom"),sQuery(id+"F0.wireOp",EDGE,"E1.left"),sQuery(id+"F0.wireOp",EDGE,"E1.right"),sQuery(id+"F0.wireOp",EDGE,"E2.bottom"),sQuery(id+"F0.wireOp",EDGE,"E2.left"),sQuery(id+"F0.wireOp",EDGE,"E2.right"),subQ2,sQuery(id+"F0.wireOp",EDGE,"E3.left"),subQ1,subQ0,sQuery(id+"F0.wireOp",EDGE,"E5.trimOffspring"),sQuery(id+"F0.wireOp",EDGE,"E6.trimOffspring")])],"isStart":true})])],"derivedFrom":makeQuery(id+"F1.opExtrude","SWEPT_FACE",FACE,{"disambiguationData":[OSD([subQ1])]})})]});}
            var Q19;
            {var subQ0=sQuery(id+"F0.wireOp",EDGE,"E0.bottom");var subQ1=sQuery(id+"F0.wireOp",EDGE,"E3.left");var subQ2=sQuery(id+"F0.wireOp",EDGE,"E3.bottom");var subQ3=sQuery(id+"F0.wireOp",EDGE,"E0.left");Q19=makeQuery(id+"F9.opFillet","BLEND_EDGE",EDGE,{"blendedFrom":[makeQuery(id+"F1.opExtrude","CAP_EDGE",EDGE,{"disambiguationData":[OSD([subQ3])],"isStart":true}),makeQuery(id+"F8.hole-2.boolean.opBoolean","SPLIT",FACE,{"disambiguationData":[TD([makeQuery(id+"F1.opExtrude","CAP_FACE",FACE,{"disambiguationData":[OSD([subQ0,sQuery(id+"F0.wireOp",EDGE,"E0.top"),subQ3,sQuery(id+"F0.wireOp",EDGE,"E0.right"),sQuery(id+"F0.wireOp",EDGE,"E1.bottom"),sQuery(id+"F0.wireOp",EDGE,"E1.left"),sQuery(id+"F0.wireOp",EDGE,"E1.right"),sQuery(id+"F0.wireOp",EDGE,"E2.bottom"),sQuery(id+"F0.wireOp",EDGE,"E2.left"),sQuery(id+"F0.wireOp",EDGE,"E2.right"),subQ2,subQ1,sQuery(id+"F0.wireOp",EDGE,"E3.right"),sQuery(id+"F0.wireOp",EDGE,"E4.trimOffspring"),sQuery(id+"F0.wireOp",EDGE,"E5.trimOffspring"),sQuery(id+"F0.wireOp",EDGE,"E6.trimOffspring")])],"isStart":true})])],"derivedFrom":makeQuery(id+"F1.opExtrude","SWEPT_FACE",FACE,{"disambiguationData":[OSD([subQ1])]})})],"blendedInto":[makeQuery(id+"F8.hole-2.boolean.opBoolean","SPLIT",FACE,{"disambiguationData":[TD([makeQuery(id+"F1.opExtrude","CAP_FACE",FACE,{"disambiguationData":[OSD([subQ0,sQuery(id+"F0.wireOp",EDGE,"E0.top"),subQ3,sQuery(id+"F0.wireOp",EDGE,"E0.right"),sQuery(id+"F0.wireOp",EDGE,"E1.bottom"),sQuery(id+"F0.wireOp",EDGE,"E1.left"),sQuery(id+"F0.wireOp",EDGE,"E1.right"),sQuery(id+"F0.wireOp",EDGE,"E2.bottom"),sQuery(id+"F0.wireOp",EDGE,"E2.left"),sQuery(id+"F0.wireOp",EDGE,"E2.right"),subQ2,subQ1,sQuery(id+"F0.wireOp",EDGE,"E3.right"),sQuery(id+"F0.wireOp",EDGE,"E4.trimOffspring"),sQuery(id+"F0.wireOp",EDGE,"E5.trimOffspring"),sQuery(id+"F0.wireOp",EDGE,"E6.trimOffspring")])],"isStart":true})])],"derivedFrom":makeQuery(id+"F1.opExtrude","SWEPT_FACE",FACE,{"disambiguationData":[OSD([subQ1])]})})]});}
            var Q20;
            Q20=makeQuery(id+"F8.hole-2.boolean.opBoolean","INTERSECT",EDGE,{"disambiguationData":[OD(1.0)],"derivedFrom":[makeQuery(id+"F1.opExtrude","SWEPT_FACE",FACE,{"disambiguationData":[OSD([sQuery(id+"F0.wireOp",EDGE,"E3.left")])]}),makeQuery(id+"F8.hole-2.opRevolve","SWEPT_FACE",FACE,{"disambiguationData":[OSD([sQuery(id+"F8.hole-2.sketch.wireOp",EDGE,"core_line_2")])]})]});
            var Q21;
            Q21=makeQuery(id+"F8.hole-1.boolean.opBoolean","INTERSECT",EDGE,{"disambiguationData":[OD(1.0)],"derivedFrom":[makeQuery(id+"F1.opExtrude","SWEPT_FACE",FACE,{"disambiguationData":[OSD([sQuery(id+"F0.wireOp",EDGE,"E1.right")])]}),makeQuery(id+"F8.hole-1.opRevolve","SWEPT_FACE",FACE,{"disambiguationData":[OSD([sQuery(id+"F8.hole-1.sketch.wireOp",EDGE,"core_line_2")])]})]});
            var Q22;
            Q22=makeQuery(id+"F8.hole-1.boolean.opBoolean","INTERSECT",EDGE,{"disambiguationData":[OD(0.0)],"derivedFrom":[makeQuery(id+"F1.opExtrude","SWEPT_FACE",FACE,{"disambiguationData":[OSD([sQuery(id+"F0.wireOp",EDGE,"E1.right")])]}),makeQuery(id+"F8.hole-1.opRevolve","SWEPT_FACE",FACE,{"disambiguationData":[OSD([sQuery(id+"F8.hole-1.sketch.wireOp",EDGE,"core_line_2")])]})]});
            var Q23;
            Q23=makeQuery(id+"F8.hole-2.boolean.opBoolean","INTERSECT",EDGE,{"disambiguationData":[OD(0.0)],"derivedFrom":[makeQuery(id+"F1.opExtrude","SWEPT_FACE",FACE,{"disambiguationData":[OSD([sQuery(id+"F0.wireOp",EDGE,"E3.left")])]}),makeQuery(id+"F8.hole-2.opRevolve","SWEPT_FACE",FACE,{"disambiguationData":[OSD([sQuery(id+"F8.hole-2.sketch.wireOp",EDGE,"core_line_2")])]})]});
            fillet(context, id + "F10", {"entities" : qUnion([Q0, Q1, Q2, Q3, Q4, Q5, Q6, Q7, Q8, Q9, Q10, Q11, Q12, Q13, Q14, Q15, Q16, Q17, Q18, Q19, Q20, Q21, Q22, Q23]), "radius" : 2.54 * mm, "tangentPropagation" : true, "allowEdgeOverflow" : false});
        }
        {
            var Q0;
            Q0=makeQuery(id+"F5.boolean.opBoolean","INTERSECT",EDGE,{"derivedFrom":[makeQuery(id+"F1.opExtrude","SWEPT_FACE",FACE,{"disambiguationData":[OSD([sQuery(id+"F0.wireOp",EDGE,"E4.trimOffspring")])]}),makeQuery(id+"F5.opExtrude","SWEPT_FACE",FACE,{"disambiguationData":[OSD([sQuery(id+"F4.wireOp",EDGE,"E16")])]})]});
            var Q1;
            Q1=makeQuery(id+"F5.boolean.opBoolean","INTERSECT",EDGE,{"derivedFrom":[makeQuery(id+"F1.opExtrude","SWEPT_FACE",FACE,{"disambiguationData":[OSD([sQuery(id+"F0.wireOp",EDGE,"E5.trimOffspring")])]}),makeQuery(id+"F5.opExtrude","SWEPT_FACE",FACE,{"disambiguationData":[OSD([sQuery(id+"F4.wireOp",EDGE,"E13")])]})]});
            var Q2;
            Q2=makeQuery(id+"F3.boolean.opBoolean","INTERSECT",EDGE,{"derivedFrom":[makeQuery(id+"F1.opExtrude","SWEPT_FACE",FACE,{"disambiguationData":[OSD([sQuery(id+"F0.wireOp",EDGE,"E5.trimOffspring")])]}),makeQuery(id+"F3.opExtrude","SWEPT_FACE",FACE,{"disambiguationData":[OSD([sQuery(id+"F2.wireOp",EDGE,"E7")])]})]});
            var Q3;
            Q3=makeQuery(id+"F3.boolean.opBoolean","INTERSECT",EDGE,{"derivedFrom":[makeQuery(id+"F1.opExtrude","SWEPT_FACE",FACE,{"disambiguationData":[OSD([sQuery(id+"F0.wireOp",EDGE,"E4.trimOffspring")])]}),makeQuery(id+"F3.opExtrude","SWEPT_FACE",FACE,{"disambiguationData":[OSD([sQuery(id+"F2.wireOp",EDGE,"E9")])]})]});
            var Q4;
            Q4=makeQuery(id+"F1.opExtrude","SWEPT_EDGE",EDGE,{"disambiguationData":[OSD([sQuery(id+"F0.wireOp",EDGE,"E0.bottom"),sQuery(id+"F0.wireOp",EDGE,"E0.left")])]});
            var Q5;
            Q5=makeQuery(id+"F1.opExtrude","SWEPT_EDGE",EDGE,{"disambiguationData":[OSD([sQuery(id+"F0.wireOp",EDGE,"E0.right"),sQuery(id+"F0.wireOp",EDGE,"E6.trimOffspring")])]});
            var Q6;
            {var subQ0=sQuery(id+"F0.wireOp",EDGE,"E3.right");var subQ1=sQuery(id+"F0.wireOp",EDGE,"E3.left");var subQ2=sQuery(id+"F0.wireOp",EDGE,"E3.bottom");Q6=makeQuery(id+"F8.hole-2.boolean.opBoolean","SPLIT",FACE,{"disambiguationData":[TD([makeQuery(id+"F1.opExtrude","CAP_FACE",FACE,{"disambiguationData":[OSD([sQuery(id+"F0.wireOp",EDGE,"E0.bottom"),sQuery(id+"F0.wireOp",EDGE,"E0.top"),sQuery(id+"F0.wireOp",EDGE,"E0.left"),sQuery(id+"F0.wireOp",EDGE,"E0.right"),sQuery(id+"F0.wireOp",EDGE,"E1.bottom"),sQuery(id+"F0.wireOp",EDGE,"E1.left"),sQuery(id+"F0.wireOp",EDGE,"E1.right"),sQuery(id+"F0.wireOp",EDGE,"E2.bottom"),sQuery(id+"F0.wireOp",EDGE,"E2.left"),sQuery(id+"F0.wireOp",EDGE,"E2.right"),subQ2,subQ1,subQ0,sQuery(id+"F0.wireOp",EDGE,"E4.trimOffspring"),sQuery(id+"F0.wireOp",EDGE,"E5.trimOffspring"),sQuery(id+"F0.wireOp",EDGE,"E6.trimOffspring")])],"isStart":true})])],"derivedFrom":makeQuery(id+"F1.opExtrude","SWEPT_FACE",FACE,{"disambiguationData":[OSD([subQ2])]})});}
            var Q7;
            Q7=makeQuery(id+"F8.hole-2.boolean.opBoolean","SPLIT",FACE,{"disambiguationData":[TD([makeQuery(id+"F5.boolean.opBoolean","COPY",FACE,{"derivedFrom":makeQuery(id+"F5.opExtrude","SWEPT_FACE",FACE,{"disambiguationData":[OSD([sQuery(id+"F4.wireOp",EDGE,"E16")])]})})])],"derivedFrom":makeQuery(id+"F1.opExtrude","SWEPT_FACE",FACE,{"disambiguationData":[OSD([sQuery(id+"F0.wireOp",EDGE,"E3.bottom")])]})});
            var Q8;
            Q8=makeQuery(id+"F8.hole-1.boolean.opBoolean","SPLIT",FACE,{"disambiguationData":[TD([makeQuery(id+"F3.boolean.opBoolean","COPY",FACE,{"derivedFrom":makeQuery(id+"F3.opExtrude","SWEPT_FACE",FACE,{"disambiguationData":[OSD([sQuery(id+"F2.wireOp",EDGE,"E8")])]})})])],"derivedFrom":makeQuery(id+"F1.opExtrude","SWEPT_FACE",FACE,{"disambiguationData":[OSD([sQuery(id+"F0.wireOp",EDGE,"E1.bottom")])]})});
            var Q9;
            Q9=makeQuery(id+"F8.hole-0.boolean.opBoolean","SPLIT",FACE,{"disambiguationData":[TD([makeQuery(id+"F5.boolean.opBoolean","COPY",FACE,{"derivedFrom":makeQuery(id+"F5.opExtrude","SWEPT_FACE",FACE,{"disambiguationData":[OSD([sQuery(id+"F4.wireOp",EDGE,"E12")])]})})])],"derivedFrom":makeQuery(id+"F1.opExtrude","SWEPT_FACE",FACE,{"disambiguationData":[OSD([sQuery(id+"F0.wireOp",EDGE,"E2.bottom")])]})});
            var Q10;
            {var subQ0=sQuery(id+"F0.wireOp",EDGE,"E2.right");var subQ1=sQuery(id+"F0.wireOp",EDGE,"E2.left");var subQ2=sQuery(id+"F0.wireOp",EDGE,"E2.bottom");Q10=makeQuery(id+"F8.hole-0.boolean.opBoolean","SPLIT",FACE,{"disambiguationData":[TD([makeQuery(id+"F1.opExtrude","CAP_FACE",FACE,{"disambiguationData":[OSD([sQuery(id+"F0.wireOp",EDGE,"E0.bottom"),sQuery(id+"F0.wireOp",EDGE,"E0.top"),sQuery(id+"F0.wireOp",EDGE,"E0.left"),sQuery(id+"F0.wireOp",EDGE,"E0.right"),sQuery(id+"F0.wireOp",EDGE,"E1.bottom"),sQuery(id+"F0.wireOp",EDGE,"E1.left"),sQuery(id+"F0.wireOp",EDGE,"E1.right"),subQ2,subQ1,subQ0,sQuery(id+"F0.wireOp",EDGE,"E3.bottom"),sQuery(id+"F0.wireOp",EDGE,"E3.left"),sQuery(id+"F0.wireOp",EDGE,"E3.right"),sQuery(id+"F0.wireOp",EDGE,"E4.trimOffspring"),sQuery(id+"F0.wireOp",EDGE,"E5.trimOffspring"),sQuery(id+"F0.wireOp",EDGE,"E6.trimOffspring")])],"isStart":true})])],"derivedFrom":makeQuery(id+"F1.opExtrude","SWEPT_FACE",FACE,{"disambiguationData":[OSD([subQ2])]})});}
            var Q11;
            {var subQ0=sQuery(id+"F0.wireOp",EDGE,"E1.right");var subQ1=sQuery(id+"F0.wireOp",EDGE,"E1.left");var subQ2=sQuery(id+"F0.wireOp",EDGE,"E1.bottom");Q11=makeQuery(id+"F8.hole-1.boolean.opBoolean","SPLIT",FACE,{"disambiguationData":[TD([makeQuery(id+"F1.opExtrude","CAP_FACE",FACE,{"disambiguationData":[OSD([sQuery(id+"F0.wireOp",EDGE,"E0.bottom"),sQuery(id+"F0.wireOp",EDGE,"E0.top"),sQuery(id+"F0.wireOp",EDGE,"E0.left"),sQuery(id+"F0.wireOp",EDGE,"E0.right"),subQ2,subQ1,subQ0,sQuery(id+"F0.wireOp",EDGE,"E2.bottom"),sQuery(id+"F0.wireOp",EDGE,"E2.left"),sQuery(id+"F0.wireOp",EDGE,"E2.right"),sQuery(id+"F0.wireOp",EDGE,"E3.bottom"),sQuery(id+"F0.wireOp",EDGE,"E3.left"),sQuery(id+"F0.wireOp",EDGE,"E3.right"),sQuery(id+"F0.wireOp",EDGE,"E4.trimOffspring"),sQuery(id+"F0.wireOp",EDGE,"E5.trimOffspring"),sQuery(id+"F0.wireOp",EDGE,"E6.trimOffspring")])],"isStart":false})])],"derivedFrom":makeQuery(id+"F1.opExtrude","SWEPT_FACE",FACE,{"disambiguationData":[OSD([subQ2])]})});}
            var Q12;
            Q12=makeQuery(id+"F1.opExtrude","SWEPT_EDGE",EDGE,{"disambiguationData":[OSD([sQuery(id+"F0.wireOp",EDGE,"E0.top"),sQuery(id+"F0.wireOp",EDGE,"E0.left")])]});
            var Q13;
            Q13=makeQuery(id+"F8.hole-0.boolean.opBoolean","COPY",FACE,{"derivedFrom":makeQuery(id+"F8.hole-0.opRevolve","SWEPT_FACE",FACE,{"disambiguationData":[OSD([sQuery(id+"F8.hole-0.sketch.wireOp",EDGE,"core_line_2")])]})});
            var Q14;
            Q14=makeQuery(id+"F8.hole-1.boolean.opBoolean","COPY",FACE,{"derivedFrom":makeQuery(id+"F8.hole-1.opRevolve","SWEPT_FACE",FACE,{"disambiguationData":[OSD([sQuery(id+"F8.hole-1.sketch.wireOp",EDGE,"core_line_2")])]})});
            var Q15;
            Q15=makeQuery(id+"F8.hole-2.boolean.opBoolean","COPY",FACE,{"derivedFrom":makeQuery(id+"F8.hole-2.opRevolve","SWEPT_FACE",FACE,{"disambiguationData":[OSD([sQuery(id+"F8.hole-2.sketch.wireOp",EDGE,"core_line_2")])]})});
            var Q16;
            Q16=makeQuery(id+"F7.hole-1.boolean.opBoolean","INTERSECT",EDGE,{"derivedFrom":[makeQuery(id+"F1.opExtrude","SWEPT_FACE",FACE,{"disambiguationData":[OSD([sQuery(id+"F0.wireOp",EDGE,"E0.top")])]}),makeQuery(id+"F7.hole-1.opRevolve","SWEPT_FACE",FACE,{"disambiguationData":[OSD([sQuery(id+"F7.hole-1.sketch.wireOp",EDGE,"core_line_2")])]})]});
            var Q17;
            Q17=makeQuery(id+"F7.hole-2.boolean.opBoolean","INTERSECT",EDGE,{"derivedFrom":[makeQuery(id+"F1.opExtrude","SWEPT_FACE",FACE,{"disambiguationData":[OSD([sQuery(id+"F0.wireOp",EDGE,"E0.top")])]}),makeQuery(id+"F7.hole-2.opRevolve","SWEPT_FACE",FACE,{"disambiguationData":[OSD([sQuery(id+"F7.hole-2.sketch.wireOp",EDGE,"core_line_2")])]})]});
            var Q18;
            Q18=makeQuery(id+"F7.hole-0.boolean.opBoolean","INTERSECT",EDGE,{"derivedFrom":[makeQuery(id+"F1.opExtrude","SWEPT_FACE",FACE,{"disambiguationData":[OSD([sQuery(id+"F0.wireOp",EDGE,"E0.top")])]}),makeQuery(id+"F7.hole-0.opRevolve","SWEPT_FACE",FACE,{"disambiguationData":[OSD([sQuery(id+"F7.hole-0.sketch.wireOp",EDGE,"core_line_2")])]})]});
            chamfer(context, id + "F11", {"entities" : qUnion([Q0, Q1, Q2, Q3, Q4, Q5, Q6, Q7, Q8, Q9, Q10, Q11, Q12, Q13, Q14, Q15, Q16, Q17, Q18]), "width" : 0.5 * mm, "tangentPropagation" : true});
        }
        {
            var Q0;
            Q0=makeQuery(id+"F1.opExtrude","SWEPT_FACE",FACE,{"disambiguationData":[OSD([sQuery(id+"F0.wireOp",EDGE,"E0.top")])]});
            var sketch = newSketch(context, id + "F12", { "sketchPlane" : qUnion([Q0])});
            skLineSegment(sketch, "E27", {"start": v(0, 33.4) * mm, "end": v(0.9, 34.3) * mm});
            skLineSegment(sketch, "E28", {"start": v(0.9, 34.3) * mm, "end": v(-0.9, 34.3) * mm});
            skLineSegment(sketch, "E29", {"start": v(-0.9, 34.3) * mm, "end": v(0, 33.4) * mm});
            skCircle(sketch, "E30.0", {"center": v(0, 25.4) * mm, "radius": 1.59 * mm, "construction": true});
            skSolve(sketch);
        }
        {
            var Q0;
            Q0 = qSketchRegion(id + "F12", true);
            extrude(context, id + "F13", {"entities" : qUnion([Q0]), "operationType" : NewBodyOperationType.REMOVE, "endBound" : BoundingType.THROUGH_ALL, "oppositeDirection" : true, "depth" : 25.4 * mm, "offsetDistance" : 25.4 * mm});
        }
    });
